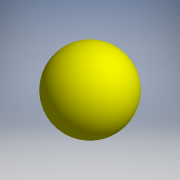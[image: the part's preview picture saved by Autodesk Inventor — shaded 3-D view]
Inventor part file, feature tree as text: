
AUTODESK INVENTOR PART (.ipt)
format: ipt  version: 2017.3 (Build 213256000, 256)  size: 118,272 bytes
history: native  units: mm (DEFAULTED — no unit token found)
features: revolve x1, sketch x1
ambient origin geometry x8: Origin, YZ Plane, XZ Plane, XY Plane, X Axis, Y Axis, Z Axis, Center Point
bodies: Solid1 (feature_tree)
feature tree (2):
  revolve  "Revolution1"  [1 undecoded]
  sketch  "Sketch_6"  dims[d0=360.0deg]
note: 1 required parameter value undecoded (feature->parameter linkage not recoverable at this tier; creation-order binding heuristic only, values carry confidence <= 0.55)
